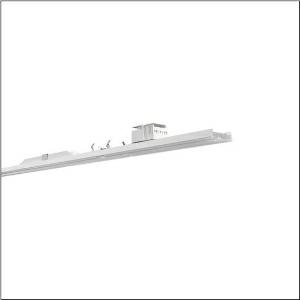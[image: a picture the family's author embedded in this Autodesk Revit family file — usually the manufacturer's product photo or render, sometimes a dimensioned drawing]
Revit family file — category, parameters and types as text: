
# Revit family: licross_r__11_recessed_mo_51tl117n48xf_17f2
name_source: partatom
category: Lighting Fixtures
units: mm (PartAtom-declared; Revit-internal decimal feet)

## family parameters
Cut with Voids When Loaded = No
Host = Face
Light Source = No
Part Type = Normal
Room Calculation Point = No
Round Connector Dimension = Use Diameter
Shared = No

## types (1)
- Licross® 11 Recessed MO (1 x LED, 8240 lm, 47.6 W, 4000K)
    Apparent Load = 48 VA
    CIE Flux Codes = 89 96 99 100 100
    Color Rendering = 80
    Color Temperature = 4000K
    Default Elevation = 1800 mm
    Description = Licross® 11 Recessed MOluminaire insert, length: 1.500mm, width: 66mm, height: 67mm, LED rated luminous flux: 8.240lm, light colour: 840, control gear: ON/OFF, control gear: ECG, with plug, 3-pole, with phase selection, mains connection: 220..240V, AC, 50/60Hz, halogen-free wiring, primary optical cover: cover, of PMMA, light emission: direct distribution, protection rating (complete): IP40, insulation class (complete): insulation class I (protective earthing), certification: CE, ENEC, VDE, protection symbol: D if used in an environment without relevant dust loads with corresponding accessories, permissible ambient temperature for indoor applications: -35..+40°C, reducing of maximum allowable ambient temperature of 5°C with ceiling mounting, corresponds to IFS (International Featured Standards) requirements for safety and quality in the food industry, packaging unit: 1 piece
    Height = 58 mm
    Lamp = 1 x LED
    Lamp Light Flux = 8240 lm
    Lamp Power = 47.6 W
    Lamp count = 1
    Length = 1500 mm
    Luminous efficacy = 173 lm/W
    Manufacturer = Siteco
    ModVariant = No
    Model = 51TL117N48XF
    Mounting Place = Ceiling
    Mounting Type = Pendant
    Number of Poles = 1
    OnlyDefault = Yes
    Power Factor = 1
    Product Name = Licross® 11 Recessed MO
    Product group = luminaire insert
    ProductGroupID = 902
    Protection Class = Protection class I
    Protection Degree = IP 40
    RLX_Detail_Level = 1
    RlxData = <blob elided: 18669 chars, md5=5d45a773>
    Socket = socket
    Standby Power = 0 W
    System Light Flux = 8240 lm
    System Power = 48 W
    Type Comments = Product without accessories
    Type Image = l_1266722.jpg
    URL = http://relux.com
    VarID = ---
    Voltage = 0 V
    Weight = 0.00 kg
    Width = 66 mm

## geometry (parser evidence)
native form markers: Blend x4, Sweep x12
no freeform markers — native parametric forms only
